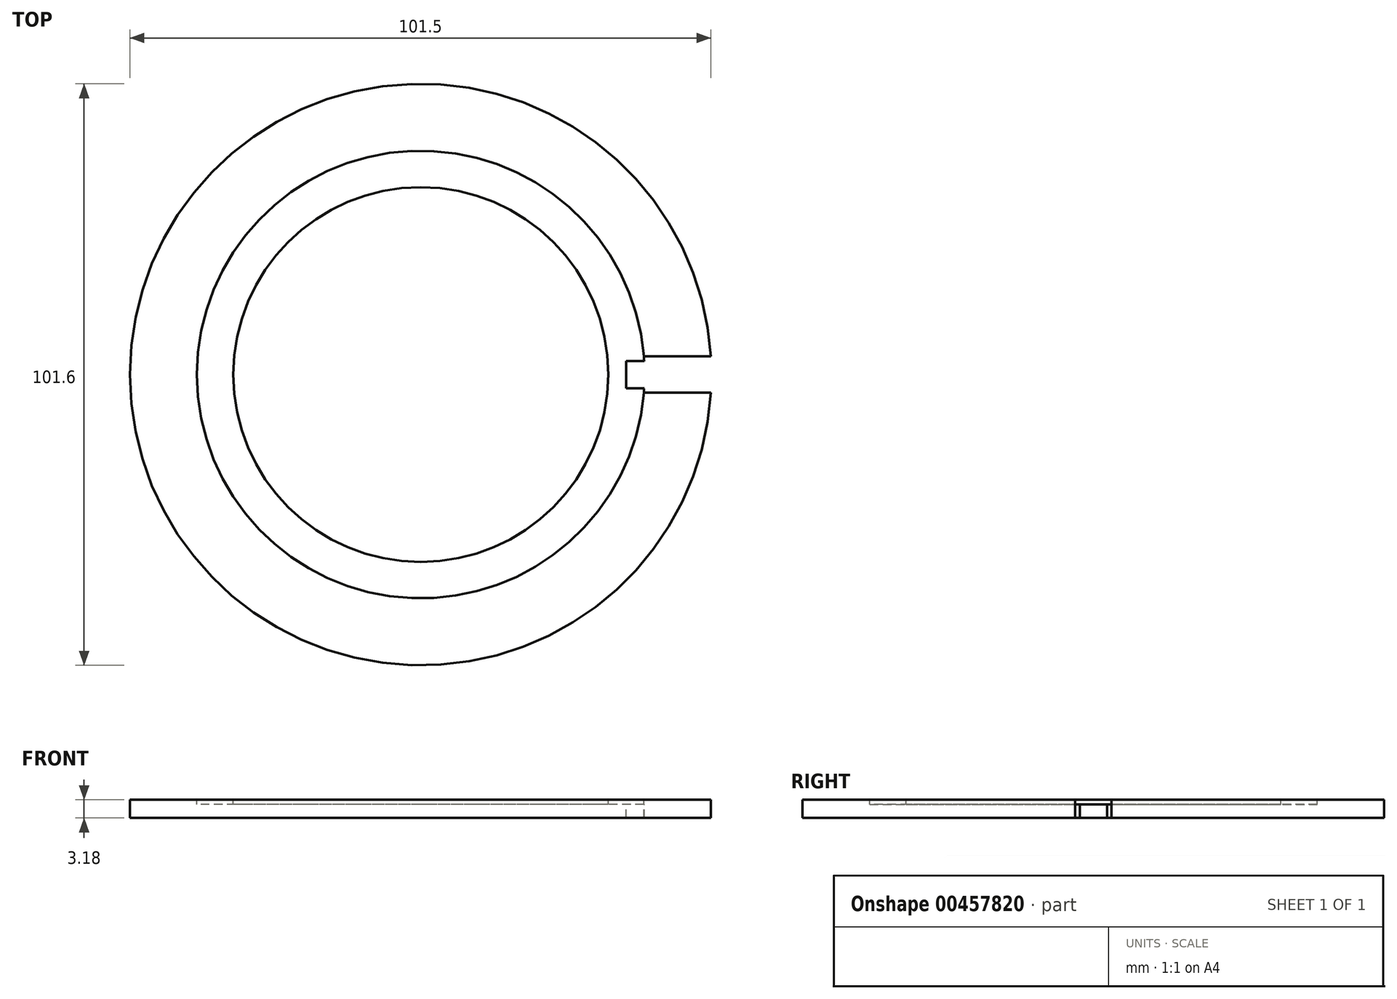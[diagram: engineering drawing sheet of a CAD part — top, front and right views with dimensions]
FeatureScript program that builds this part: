
annotation { "Feature Type Name" : "Feature", "Feature Type Description" : "" }
export const myFeature = defineFeature(function(context is Context, id is Id, definition is map)
    precondition{}
    {
        {
            var Q0;
            Q0=qCreatedBy(makeId("Top.planeOp"),FACE);
            var sketch = newSketch(context, id + "F0", { "sketchPlane" : qUnion([Q0])});
            skArc(sketch, "E0", {"start": v(50.7, 3.18) * mm, "mid": v(-50.8, 0) * mm, "end": v(50.7, -3.17) * mm});
            skLineSegment(sketch, "E1.0", {"start": v(50.7, 3.18) * mm, "end": v(35.85, 3.17) * mm});
            skLineSegment(sketch, "E2.0", {"start": v(50.7, -3.17) * mm, "end": v(35.85, -3.18) * mm});
            skLineSegment(sketch, "E3", {"start": v(35.85, 3.17) * mm, "end": v(35.85, -3.18) * mm});
            skPoint(sketch, "E4.start.orphan", {"position": v(50.8, 0) * mm});
            skLineSegment(sketch, "E5", {"start": v(50.8, 0) * mm, "end": v(0, 0) * mm, "construction": true});
            skSolve(sketch);
        }
        {
            var Q0;
            Q0=makeQuery(id+"F0.imprint","IMPRINT",FACE,{"disambiguationData":[TD([[makeQuery(id+"F0.imprint","IMPRINT",EDGE,{"derivedFrom":sQuery(id+"F0.wireOp",EDGE,"E0")}),1.0]])]});
            extrude(context, id + "F1", {"entities" : qUnion([Q0]), "depth" : 3.17 * mm});
        }
        {
            var Q0;
            Q0=makeQuery(id+"F1.opExtrude","CAP_FACE",FACE,{"disambiguationData":[OSD([sQuery(id+"F0.wireOp",EDGE,"E0"),sQuery(id+"F0.wireOp",EDGE,"E1.0"),sQuery(id+"F0.wireOp",EDGE,"E2.0"),sQuery(id+"F0.wireOp",EDGE,"E3")])],"isStart":false});
            var sketch = newSketch(context, id + "F2", { "sketchPlane" : qUnion([Q0])});
            skArc(sketch, "E6.0", {"start": v(39.08, 1.22) * mm, "mid": v(-39.1, 0) * mm, "end": v(39.08, -1.22) * mm});
            skCircle(sketch, "E7", {"center": v(0, 0) * mm, "radius": 32.75 * mm});
            skSolve(sketch);
        }
        {
            var Q0;
            {var subQ0=sQuery(id+"F2.wireOp",EDGE,"7e539c9c-dfe4-4d2e-a318-fa9bffde27fd.0");var subQ1=makeQuery(id+"F1.opExtrude","CAP_EDGE",EDGE,{"disambiguationData":[OSD([sQuery(id+"F0.wireOp",EDGE,"E1.0")])],"isStart":false});var subQ2=makeQuery(id+"F2.imprint","INTERSECT",VERTEX,{"derivedFrom":[subQ1,subQ0]});Q0=makeQuery(id+"F2.imprint","IMPRINT",FACE,{"disambiguationData":[TD([[makeQuery(id+"F2.imprint","IMPRINT",EDGE,{"disambiguationData":[TD([[subQ2,-1.0]])],"derivedFrom":subQ0}),-1.0]])]});}
            var Q1;
            Q1=makeQuery(id+"F2.imprint","IMPRINT",FACE,{"disambiguationData":[TD([[makeQuery(id+"F2.imprint","IMPRINT",EDGE,{"derivedFrom":sQuery(id+"F2.wireOp",EDGE,"E7")}),-1.0]])]});
            extrude(context, id + "F3", {"entities" : qUnion([Q0, Q1]), "operationType" : NewBodyOperationType.REMOVE, "oppositeDirection" : true, "depth" : 0.8 * mm});
        }
        {
            var Q0;
            Q0=makeQuery(id+"F3.boolean.opBoolean","COPY",FACE,{"derivedFrom":makeQuery(id+"F3.opExtrude","CAP_FACE",FACE,{"disambiguationData":[OSD([sQuery(id+"F0.wireOp",EDGE,"E1.0"),sQuery(id+"F0.wireOp",EDGE,"E2.0"),sQuery(id+"F0.wireOp",EDGE,"E3"),sQuery(id+"F2.wireOp",EDGE,"E6.0"),sQuery(id+"F2.wireOp",EDGE,"E7")])],"isStart":false})});
            var sketch = newSketch(context, id + "F4", { "sketchPlane" : qUnion([Q0])});
            skLineSegment(sketch, "E8.0", {"start": v(39.02, 2.38) * mm, "end": v(35.85, 2.38) * mm});
            skLineSegment(sketch, "E9.0", {"start": v(39.02, -2.38) * mm, "end": v(35.85, -2.38) * mm});
            skArc(sketch, "E10", {"start": v(38.97, -3.17) * mm, "mid": v(39, -2.78) * mm, "end": v(39.02, -2.38) * mm});
            skArc(sketch, "E11.trimOffspring", {"start": v(39.02, 2.38) * mm, "mid": v(39, 2.78) * mm, "end": v(38.97, 3.18) * mm});
            skLineSegment(sketch, "E12.0", {"start": v(35.85, 3.17) * mm, "end": v(35.85, -3.18) * mm});
            skSolve(sketch);
        }
        {
            var Q0;
            {var subQ0=sQuery(id+"F4.wireOp",EDGE,"E9.0");Q0=makeQuery(id+"F4.imprint","IMPRINT",FACE,{"disambiguationData":[TD([[makeQuery(id+"F4.imprint","IMPRINT",EDGE,{"derivedFrom":subQ0}),1.0]])]});}
            var Q1;
            {var subQ0=sQuery(id+"F4.wireOp",EDGE,"E8.0");Q1=makeQuery(id+"F4.imprint","IMPRINT",FACE,{"disambiguationData":[TD([[makeQuery(id+"F4.imprint","IMPRINT",EDGE,{"derivedFrom":subQ0}),-1.0]])]});}
            var Q2;
            Q2=makeQuery(id+"F1.opExtrude","CAP_FACE",FACE,{"disambiguationData":[OSD([sQuery(id+"F0.wireOp",EDGE,"E0"),sQuery(id+"F0.wireOp",EDGE,"E1.0"),sQuery(id+"F0.wireOp",EDGE,"E2.0"),sQuery(id+"F0.wireOp",EDGE,"E3")])],"isStart":true});
            extrude(context, id + "F5", {"entities" : qUnion([Q0, Q1]), "operationType" : NewBodyOperationType.ADD, "endBound" : BoundingType.UP_TO_SURFACE, "oppositeDirection" : true, "endBoundEntityFace" : qUnion([Q2]), "depth" : 25.4 * mm});
        }
    });
